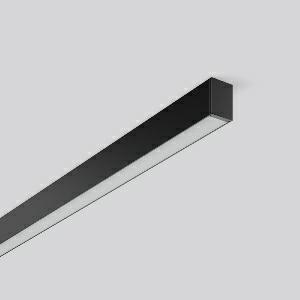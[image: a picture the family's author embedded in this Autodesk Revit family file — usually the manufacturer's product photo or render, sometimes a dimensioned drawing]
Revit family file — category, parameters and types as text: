
# Revit family: less_is_more_27_312201_003_76_e80e
name_source: partatom
category: Lighting Fixtures
units: mm (PartAtom-declared; Revit-internal decimal feet)

## family parameters
Cut with Voids When Loaded = No
Host = Face
Light Source = No
Part Type = Normal
Room Calculation Point = No
Round Connector Dimension = Use Diameter
Shared = No

## types (1)
- LESS IS MORE 27 (1 x LED Modul 830, 2750 lm, 3000)
    Apparent Load = 43 VA
    CIE Flux Codes = 65 89 98 100 100
    Color Rendering = 80
    Color Temperature = 3000
    Default Elevation = 1800 mm
    Description = Series: LESS IS MORE 27
Ceiling luminaire with slim design. Housing: extruded aluminium profile, powder-coated. End cap aluminium powder-coated. Diffuser made of non-yellowing plastic (PMMA) microprismatic. Suitable for Ceiling mounting, Wall (surface). External driver with connecting cable. 
Colour: deep black, matt (RAL 9005)
Length: 1512 mm
Width: 28 mm
Height: 38 mm
Lamp: LED
Socket: without socket
Colour temperature: 3000K
Colour rendering index (CRI): 82
System power: 43 W
Rated luminous flux: 2750 lm
Luminous efficiency: 64 lm/W
Control gear: Voltage converter, DALI dim.
Protection class: II
Type of protection: IP 20
    Height = 38 mm
    Lamp = 1 x LED Modul 830
    Lamp Light Flux = 2750 lm
    Lamp count = 1
    Length = 1512 mm
    Lifetime = 50000 h
    Luminous efficacy = 64 lm/W
    Manufacturer = RZB
    ModVariant = No
    Model = 312201.003.76
    Mounting Place = Ceiling, Wall
    Mounting Type = Surface mounted
    Number of Poles = 1
    OnlyDefault = Yes
    Power Factor = 1
    Product Name = LESS IS MORE 27
    Product group = Surface mounted LED linear luminaires
    ProductGroupID = 307
    Protection Class = Protection class II
    Protection Degree = IP 20
    RLX_Detail_Level = 1
    RLX_Emergency_Light_Flux = 0 lm
    RLX_Emergency_Type = 0
    RLX_Emergency_Type_DB = No
    RlxData = <blob elided: 29721 chars, md5=5545d2eb>
    Socket = socket
    Standby Power = 0 W
    System Light Flux = 2750 lm
    System Power = 43 W
    Type Comments = Product without accessories
    Type Image = 312197.003.jpg
    URL = http://relux.com
    VarID = ---
    Voltage = 230 V
    Voltage Range = 220-240 V
    Weight = 0.00 kg
    Width = 28 mm

## geometry (parser evidence)
native form markers: Blend x4, Sweep x11
no freeform markers — native parametric forms only
